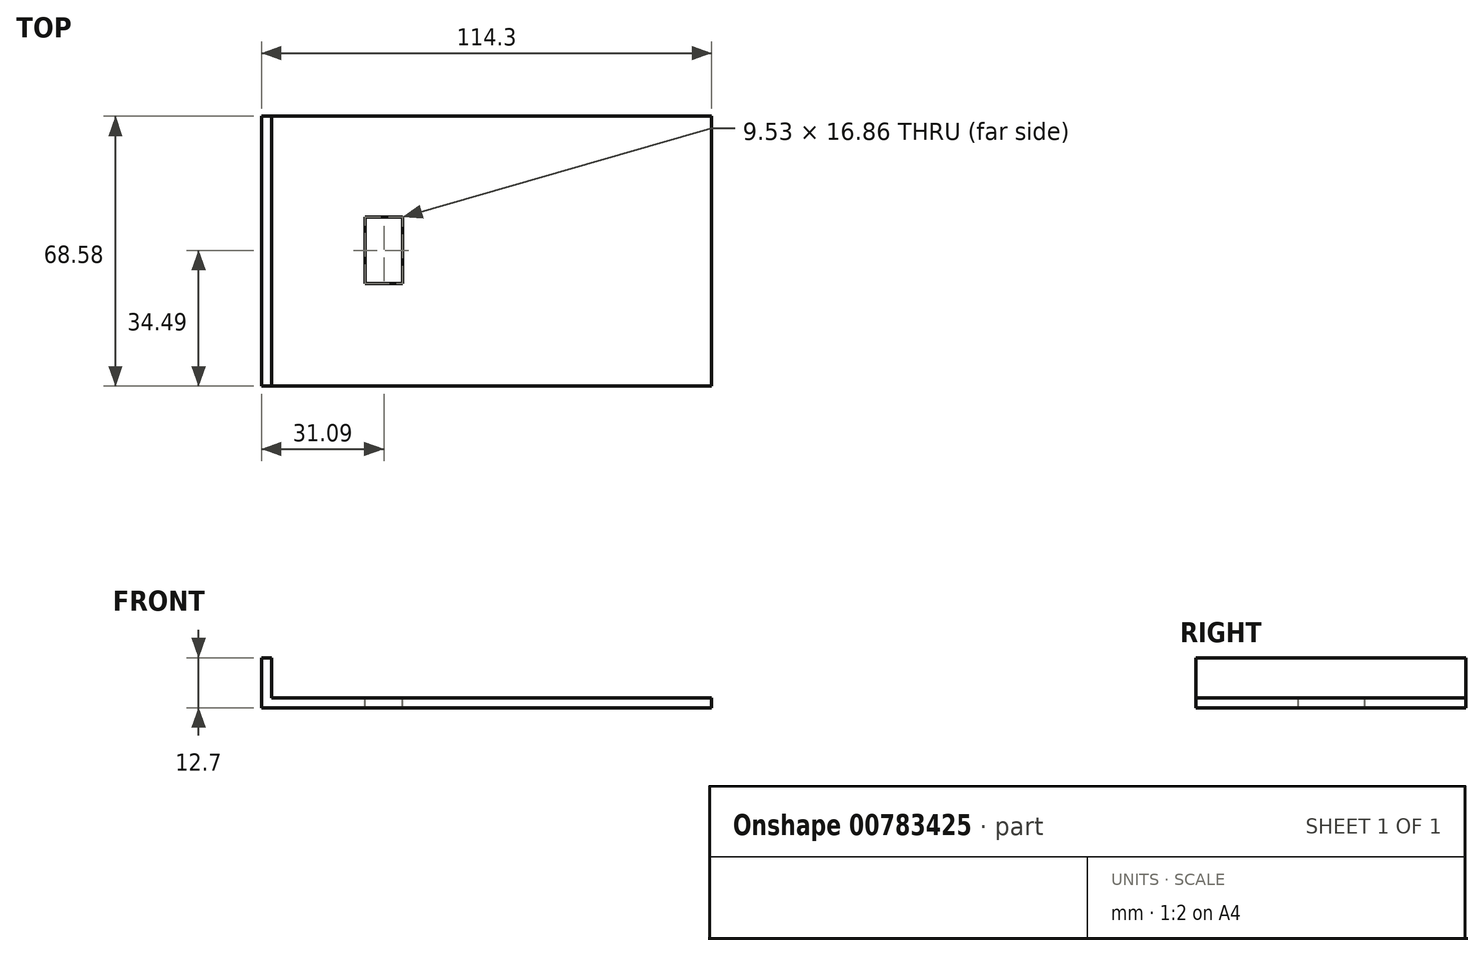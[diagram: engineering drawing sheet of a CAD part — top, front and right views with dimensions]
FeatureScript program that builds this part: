
annotation { "Feature Type Name" : "Feature", "Feature Type Description" : "" }
export const myFeature = defineFeature(function(context is Context, id is Id, definition is map)
    precondition{}
    {
        {
            var Q0;
            Q0=qCreatedBy(makeId("Top.planeOp"),FACE);
            var sketch = newSketch(context, id + "F0", { "sketchPlane" : qUnion([Q0])});
            skLineSegment(sketch, "E0.bottom", {"start": v(-55.76, 42.52) * mm, "end": v(58.54, 42.52) * mm});
            skLineSegment(sketch, "E0.top", {"start": v(-55.76, -26.06) * mm, "end": v(58.54, -26.06) * mm});
            skLineSegment(sketch, "E0.left", {"start": v(-55.76, 42.52) * mm, "end": v(-55.76, -26.06) * mm});
            skLineSegment(sketch, "E0.right", {"start": v(58.54, 42.52) * mm, "end": v(58.54, -26.06) * mm});
            skSolve(sketch);
        }
        {
            var Q0;
            Q0 = qSketchRegion(id + "F0", true);
            extrude(context, id + "F1", {"entities" : qUnion([Q0]), "depth" : 2.54 * mm, "offsetDistance" : 25.4 * mm});
        }
        {
            var Q0;
            Q0=makeQuery(id+"F1.opExtrude","CAP_FACE",FACE,{"disambiguationData":[OSD([sQuery(id+"F0.wireOp",EDGE,"E0.bottom"),sQuery(id+"F0.wireOp",EDGE,"E0.top"),sQuery(id+"F0.wireOp",EDGE,"E0.left"),sQuery(id+"F0.wireOp",EDGE,"E0.right")])],"isStart":true});
            var sketch = newSketch(context, id + "F2", { "sketchPlane" : qUnion([Q0])});
            skLineSegment(sketch, "E1.bottom", {"start": v(-55.76, 26.06) * mm, "end": v(-53.22, 26.06) * mm});
            skLineSegment(sketch, "E1.top", {"start": v(-55.76, -42.52) * mm, "end": v(-53.22, -42.52) * mm});
            skLineSegment(sketch, "E1.left", {"start": v(-55.76, 26.06) * mm, "end": v(-55.76, -42.52) * mm});
            skLineSegment(sketch, "E1.right", {"start": v(-53.22, 26.06) * mm, "end": v(-53.22, -42.52) * mm});
            skSolve(sketch);
        }
        {
            var Q0;
            Q0 = qSketchRegion(id + "F2", true);
            extrude(context, id + "F3", {"entities" : qUnion([Q0]), "operationType" : NewBodyOperationType.ADD, "depth" : 0 * mm, "offsetDistance" : 25.4 * mm, "hasSecondDirection" : true, "secondDirectionOppositeDirection" : true, "secondDirectionDepth" : 12.7 * mm});
        }
        {
            var Q0;
            Q0=makeQuery(id+"F1.opExtrude","CAP_FACE",FACE,{"disambiguationData":[OSD([sQuery(id+"F0.wireOp",EDGE,"E0.bottom"),sQuery(id+"F0.wireOp",EDGE,"E0.top"),sQuery(id+"F0.wireOp",EDGE,"E0.left"),sQuery(id+"F0.wireOp",EDGE,"E0.right")])],"isStart":false});
            var sketch = newSketch(context, id + "F4", { "sketchPlane" : qUnion([Q0])});
            skLineSegment(sketch, "E2.bottom", {"start": v(-29.43, 0) * mm, "end": v(-19.9, 0) * mm});
            skLineSegment(sketch, "E2.top", {"start": v(-29.43, 16.86) * mm, "end": v(-19.9, 16.86) * mm});
            skLineSegment(sketch, "E2.left", {"start": v(-29.43, 0) * mm, "end": v(-29.43, 16.86) * mm});
            skLineSegment(sketch, "E2.right", {"start": v(-19.9, 0) * mm, "end": v(-19.9, 16.86) * mm});
            skSolve(sketch);
        }
        {
            var Q0;
            Q0 = qSketchRegion(id + "F4", true);
            extrude(context, id + "F5", {"entities" : qUnion([Q0]), "operationType" : NewBodyOperationType.REMOVE, "depth" : 0 * mm, "offsetDistance" : 25.4 * mm, "hasSecondDirection" : true, "secondDirectionOppositeDirection" : true, "secondDirectionDepth" : 2.54 * mm});
        }
    });
